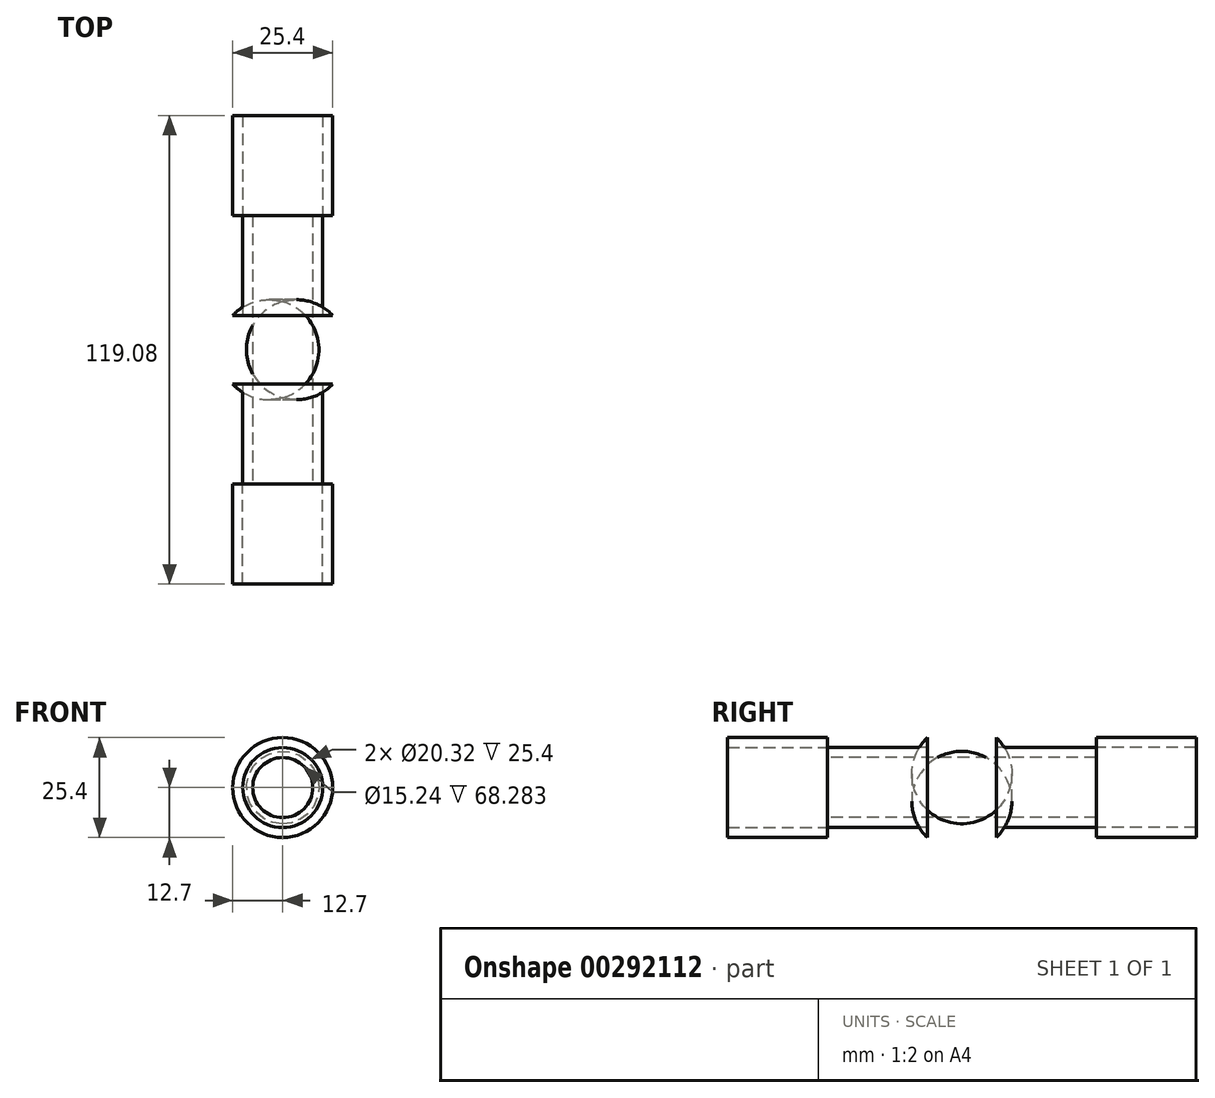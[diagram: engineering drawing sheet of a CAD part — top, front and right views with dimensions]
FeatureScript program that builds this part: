
annotation { "Feature Type Name" : "Feature", "Feature Type Description" : "" }
export const myFeature = defineFeature(function(context is Context, id is Id, definition is map)
    precondition{}
    {
        {
            var Q0;
            Q0=qCreatedBy(makeId("Front.planeOp"),FACE);
            var sketch = newSketch(context, id + "F0", { "sketchPlane" : qUnion([Q0])});
            skCircle(sketch, "E0", {"center": v(0, 0) * mm, "radius": 12.7 * mm});
            skCircle(sketch, "E1", {"center": v(0, 0) * mm, "radius": 10.16 * mm});
            skSolve(sketch);
        }
        {
            var Q0;
            Q0 = qSketchRegion(id + "F0", true);
            extrude(context, id + "F1", {"entities" : qUnion([Q0]), "depth" : 25.4 * mm});
        }
        {
            var Q0;
            Q0=qCreatedBy(makeId("Front.planeOp"),FACE);
            var sketch = newSketch(context, id + "F2", { "sketchPlane" : qUnion([Q0])});
            skCircle(sketch, "E2", {"center": v(0, 0) * mm, "radius": 10.16 * mm});
            skCircle(sketch, "E3", {"center": v(0, 0) * mm, "radius": 7.62 * mm});
            skSolve(sketch);
        }
        {
            var Q0;
            Q0 = qSketchRegion(id + "F2", true);
            extrude(context, id + "F3", {"entities" : qUnion([Q0]), "operationType" : NewBodyOperationType.ADD, "oppositeDirection" : true, "depth" : 25.4 * mm});
        }
        {
            var Q0;
            Q0=qCreatedBy(makeId("Right.planeOp"),FACE);
            var sketch = newSketch(context, id + "F4", { "sketchPlane" : qUnion([Q0])});
            skLineSegment(sketch, "E4", {"start": v(25.4, 0) * mm, "end": v(25.4, 12.7) * mm});
            skArc(sketch, "E5", {"start": v(42.88, 12.7) * mm, "mid": v(34.14, 16.19) * mm, "end": v(25.4, 12.7) * mm});
            skLineSegment(sketch, "E6", {"start": v(42.88, 12.7) * mm, "end": v(42.88, 0) * mm});
            skLineSegment(sketch, "E7", {"start": v(42.88, 0) * mm, "end": v(25.4, 0) * mm});
            skSolve(sketch);
        }
        {
            var Q0;
            Q0=makeQuery(id+"F4.imprint","IMPRINT",FACE,{"disambiguationData":[TD([[makeQuery(id+"F4.imprint","IMPRINT",EDGE,{"derivedFrom":sQuery(id+"F4.wireOp",EDGE,"E4")}),-1.0]])]});
            var Q1;
            Q1=sQuery(id+"F4.wireOp",EDGE,"E7");
            revolve(context, id + "F5", {"operationType" : NewBodyOperationType.ADD, "entities" : qUnion([Q0]), "axis" : qUnion([Q1]), "revolveType" : RevolveType.FULL});
        }
        {
            var Q0;
            Q0=makeQuery(id+"F5.opRevolve","SWEPT_FACE",FACE,{"disambiguationData":[OSD([sQuery(id+"F4.wireOp",EDGE,"E6")])]});
            var sketch = newSketch(context, id + "F6", { "sketchPlane" : qUnion([Q0])});
            skCircle(sketch, "E8", {"center": v(0, 0) * mm, "radius": 10.16 * mm});
            skCircle(sketch, "E9", {"center": v(0, 0) * mm, "radius": 7.62 * mm});
            skSolve(sketch);
        }
        {
            var Q0;
            Q0=makeQuery(id+"F6.imprint","IMPRINT",FACE,{"disambiguationData":[TD([[makeQuery(id+"F6.imprint","IMPRINT",EDGE,{"derivedFrom":sQuery(id+"F6.wireOp",EDGE,"E9")}),1.0]])]});
            extrude(context, id + "F7", {"entities" : qUnion([Q0]), "operationType" : NewBodyOperationType.REMOVE, "oppositeDirection" : true, "depth" : 25.4 * mm});
        }
        {
            var Q0;
            Q0 = qSketchRegion(id + "F6", true);
            extrude(context, id + "F8", {"entities" : qUnion([Q0]), "operationType" : NewBodyOperationType.ADD, "depth" : 25.4 * mm});
        }
        {
            var Q0;
            Q0=makeQuery(id+"F8.opExtrude","CAP_FACE",FACE,{"disambiguationData":[OSD([sQuery(id+"F6.wireOp",EDGE,"E8"),sQuery(id+"F6.wireOp",EDGE,"E9")])],"isStart":false});
            var sketch = newSketch(context, id + "F9", { "sketchPlane" : qUnion([Q0])});
            skCircle(sketch, "E10", {"center": v(0, 0) * mm, "radius": 10.16 * mm});
            skCircle(sketch, "E11", {"center": v(0, 0) * mm, "radius": 12.7 * mm});
            skSolve(sketch);
        }
        {
            var Q0;
            Q0 = qSketchRegion(id + "F9", true);
            extrude(context, id + "F10", {"entities" : qUnion([Q0]), "depth" : 25.4 * mm});
        }
    });
